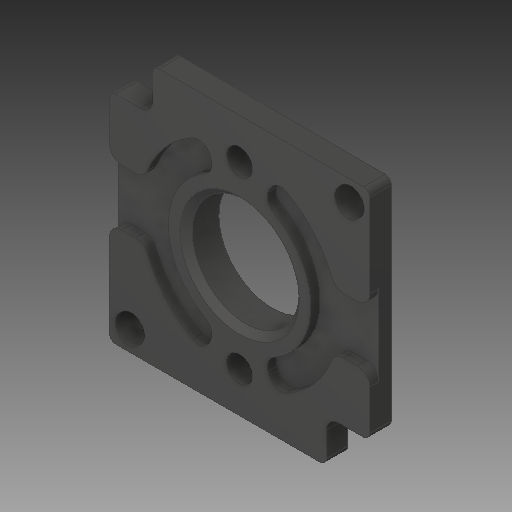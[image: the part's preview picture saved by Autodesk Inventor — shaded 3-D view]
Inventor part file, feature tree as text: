
AUTODESK INVENTOR PART (.ipt)
format: ipt  version: 2017 (Build 210142000, 142)  size: 275,456 bytes
history: native  units: in
note: dims shown in document units (in); Inventor stores cm internally (conversion verified against a paired STEP export)
features: fillet x1
ambient origin geometry x8: Origin, YZ Plane, XZ Plane, XY Plane, X Axis, Y Axis, Z Axis, Center Point
bodies: Solid1 (feature_tree)
feature tree (1):
  fillet  "Fillet4"  [1 undecoded]
note: 1 required parameter value undecoded (feature->parameter linkage not recoverable at this tier; creation-order binding heuristic only, values carry confidence <= 0.55)
